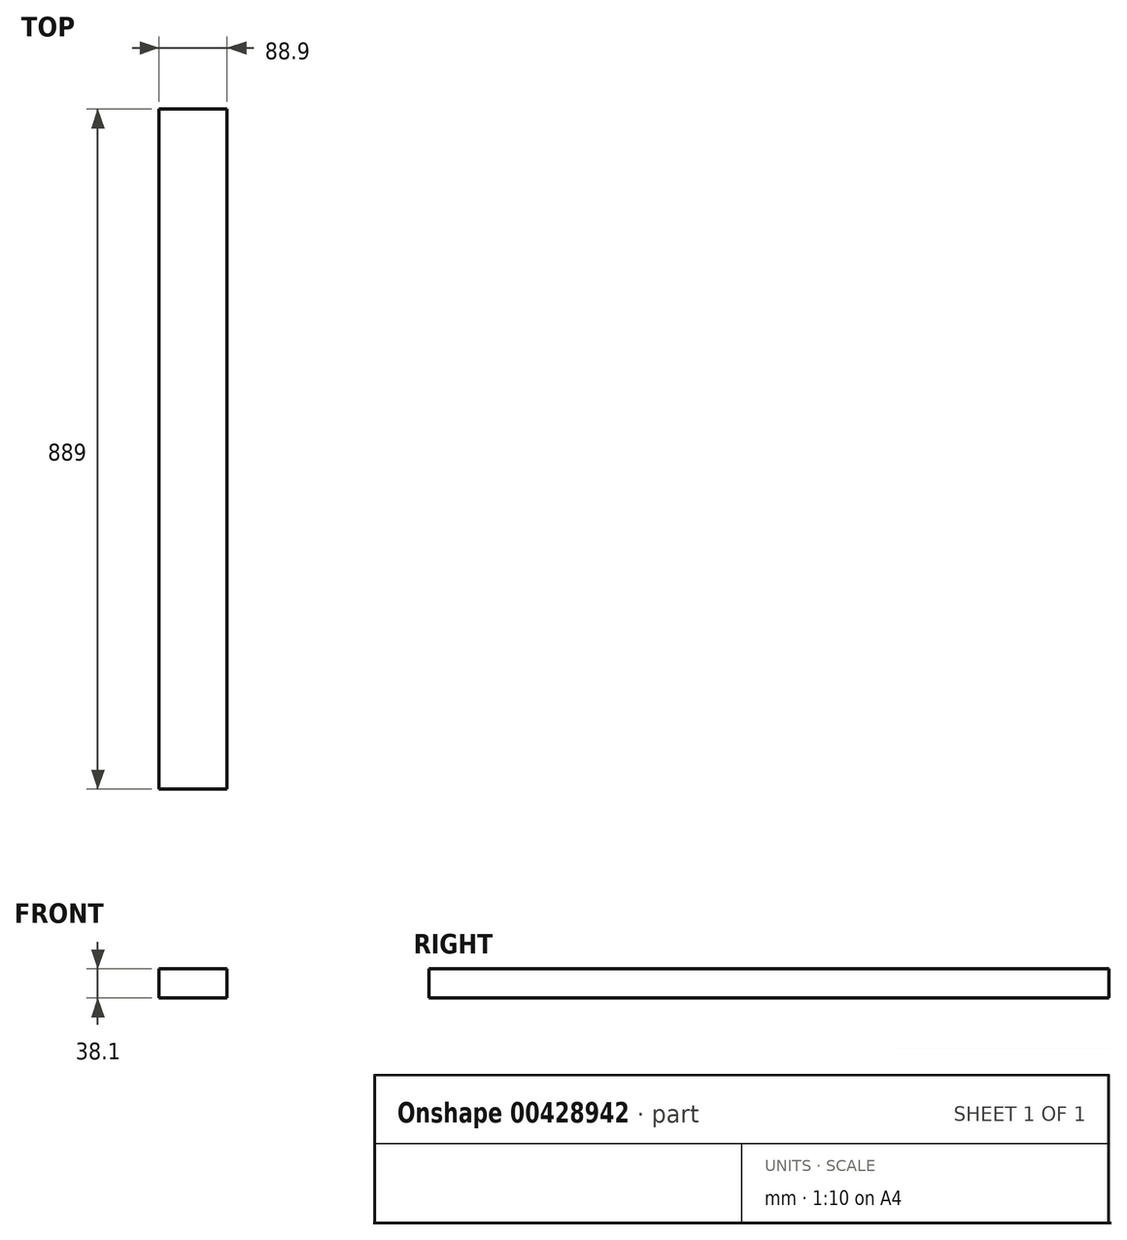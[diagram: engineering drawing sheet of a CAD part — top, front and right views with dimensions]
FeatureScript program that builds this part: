
annotation { "Feature Type Name" : "Feature", "Feature Type Description" : "" }
export const myFeature = defineFeature(function(context is Context, id is Id, definition is map)
    precondition{}
    {
        {
            var Q0;
            Q0=qCreatedBy(makeId("Top.planeOp"),FACE);
            var sketch = newSketch(context, id + "F0", { "sketchPlane" : qUnion([Q0])});
            skLineSegment(sketch, "E0.bottom", {"start": v(15.82, -115.8) * mm, "end": v(-73.08, -115.8) * mm});
            skLineSegment(sketch, "E0.top", {"start": v(15.82, 773.2) * mm, "end": v(-73.08, 773.2) * mm});
            skLineSegment(sketch, "E0.left", {"start": v(15.82, -115.8) * mm, "end": v(15.82, 773.2) * mm});
            skLineSegment(sketch, "E0.right", {"start": v(-73.08, -115.8) * mm, "end": v(-73.08, 773.2) * mm});
            skSolve(sketch);
        }
        {
            var Q0;
            Q0=makeQuery(id+"F0.imprint","IMPRINT",FACE,{"disambiguationData":[TD([[makeQuery(id+"F0.imprint","IMPRINT",EDGE,{"derivedFrom":sQuery(id+"F0.wireOp",EDGE,"E0.bottom")}),-1.0]])]});
            extrude(context, id + "F1", {"entities" : qUnion([Q0]), "depth" : 38.1 * mm});
        }
    });
